# Revit family: Bathtub-American_Standard-Town_Square-2742_Series
name_source: partatom
category: Plumbing Fixtures
revit_build: Autodesk Revit 2014 (Build: 20130308_1515(x64)
units: mm (PartAtom-declared; Revit-internal decimal feet)

## types (5) — shared parameters
Assembly Code = D2010510
CW Connection = Yes
CWFU = 3
Default Elevation = 0"
Front Offset = 3 1/2"
HW Connection = Yes
HWFU = 3
Height = 22"
Length = 41 3/4"
Manufacturer = American Standard
Outlet Diameter = 1 1/2"
Outlet Location = 13 1/4"
Product Documentation Link = https://www.americanstandard-us.com
Product Page URL = https://www.americanstandard-us.com
Revised Date = 01/17/2019
URL = https://www.americanstandard-us.com
Vent Connection = No
WFU = 4
Waste Connection = Yes
Width = 71 1/2"

## per-type parameters (varying)
| type | Description | EverClean | Finish | Material |
| 2742.002.020 | Town Square 72 Inch by 42 Inch Bathtub | No | Americast-American Standard-020-White | Americast-American Standard-020-White |
| 2742.002.222 | Town Square 72 Inch by 42 Inch Bathtub | No | Americast-American Standard-222-Linen | Americast-American Standard-222-Linen |
| 2742.068C.020 | Town Square 72 Inch by 42 Inch EverClean Air Bath | Yes | Americast-American Standard-020-White | Americast-American Standard-020-White |
| 2742.068C.K2.020 | Town Square 72 Inch by 42 Inch EverClean Air Bath | Yes | Americast-American Standard-020-White | Americast-American Standard-020-White |
| 2742.002.011 | Town Square 72 Inch by 42 Inch Bathtub | No | Americast-American Standard-011-Arctic | Americast-American Standard-011-Arctic |

note: column(s) folded — value = type name in every type: Model

## geometry (parser evidence)
native form markers: Sweep x1
no freeform markers — native parametric forms only
